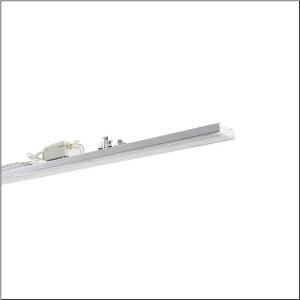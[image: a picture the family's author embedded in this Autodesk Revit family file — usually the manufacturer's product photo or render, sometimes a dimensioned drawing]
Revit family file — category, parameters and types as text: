
# Revit family: licross_r__21_recessed_mo_52tl1edn48xg_af32
name_source: partatom
category: Lighting Fixtures
units: mm (PartAtom-declared; Revit-internal decimal feet)

## family parameters
Cut with Voids When Loaded = No
Host = Face
Light Source = No
Part Type = Normal
Room Calculation Point = No
Round Connector Dimension = Use Diameter
Shared = No

## types (1)
- --- (1 x LED, 8000 lm, 45.8 W, 4000K)
    Apparent Load = 46 VA
    CIE Flux Codes = 85 95 99 100 100
    Color Rendering = 80
    Color Temperature = 4000K
    Default Elevation = 1800 mm
    Description = Licross® 21 Recessed MO, luminaire insert, of sheet steel, galvanised, coil coated, white, length: 1.500mm, width: 66mm, height: 67mm, LED rated luminous flux: 8.000lm, light colour: 840, control gear: DALI 2, with plug, 5-pole, with phase selection, mains connection: 220..240V, AC, 50/60Hz, rated input power: 46W, halogen-free wiring, primary light control with lens, of plastic, primary optical cover: cover, of PMMA, light emission: direct distribution, primary light characteristic: symmetric, protection rating (complete): IP40, insulation class (complete): insulation class I (protective earthing), certification: CE, ENEC, VDE, UKCA, protection symbol: D if used in an environment without relevant dust loads with corresponding accessories, impact resistance: IK06, permissible ambient temperature for indoor applications: -25..+40°C, corresponds to IFS (International Featured Standards) requirements for safety and quality in the food industry, reducing of maximum allowable ambient temperature of 5°C with ceiling mounting, LABS conformity tested according to VDMA 24364:2018-05, packaging unit: 1 piece
    Height = 58 mm
    Lamp = 1 x LED
    Lamp Light Flux = 8000 lm
    Lamp Power = 45.8 W
    Lamp count = 1
    Length = 1500 mm
    Luminous efficacy = 175 lm/W
    Manufacturer = Siteco
    ModVariant = No
    Model = 52TL1EDN48XG
    Mounting Place = Ceiling
    Mounting Type = Pendant
    Number of Poles = 1
    OnlyDefault = Yes
    Power Factor = 1
    Product Name = Licross® 21 Recessed MO
    Product group = luminaire insert
    ProductGroupID = 901
    Protection Class = Protection class I
    Protection Degree = IP 40
    RLX_Detail_Level = 1
    RLX_Emergency_Light_Flux = 0 lm
    RLX_Emergency_Type = 0
    RLX_Emergency_Type_DB = No
    RlxData = <blob elided: 24649 chars, md5=c2b613ce>
    Socket = socket
    Standby Power = 0 W
    System Light Flux = 8000 lm
    System Power = 46 W
    Type Comments = factory setting: luminous flux: 100 % | dim-lin: 254 | 308 mA
    Type Image = l_1296930.jpg
    URL = http://relux.com
    VarID = @adj_056797
    Voltage = 0 V
    Weight = 0.00 kg
    Width = 66 mm

## geometry (parser evidence)
native form markers: Blend x4, Sweep x11
no freeform markers — native parametric forms only
